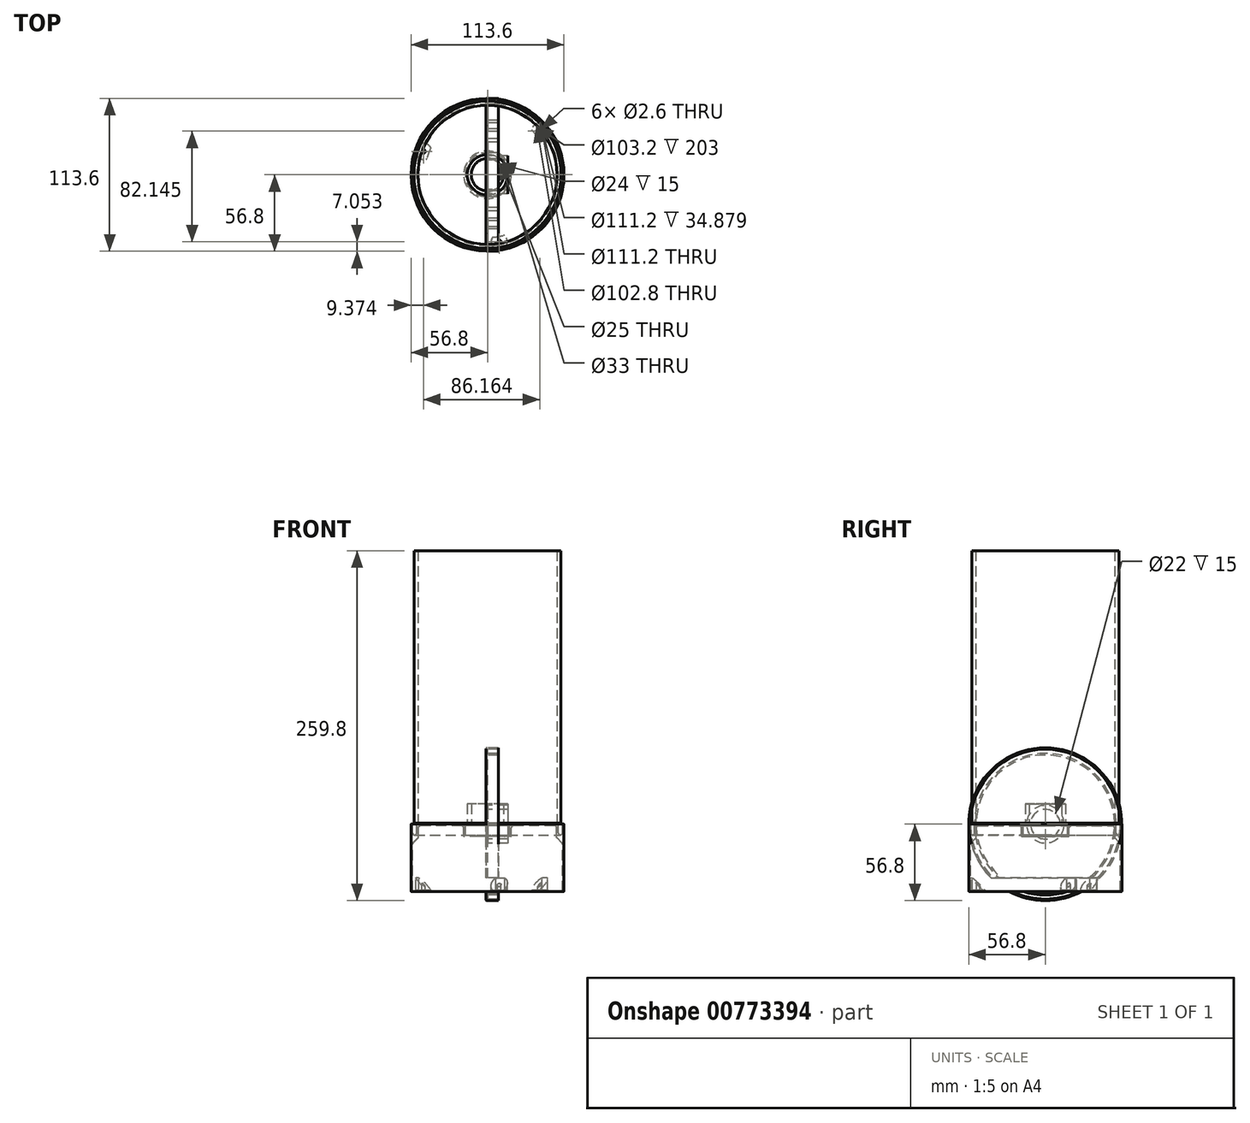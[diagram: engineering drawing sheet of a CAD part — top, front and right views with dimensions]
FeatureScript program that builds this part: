
annotation { "Feature Type Name" : "Feature", "Feature Type Description" : "" }
export const myFeature = defineFeature(function(context is Context, id is Id, definition is map)
    precondition{}
    {
        {
            var Q0;
            Q0=qCreatedBy(makeId("Front.planeOp"),FACE);
            var sketch = newSketch(context, id + "F0", { "sketchPlane" : qUnion([Q0])});
            skLineSegment(sketch, "E0", {"start": v(-56.8, 0) * mm, "end": v(-55.6, 0) * mm});
            skLineSegment(sketch, "E1", {"start": v(-55.6, 0) * mm, "end": v(-55.6, -8) * mm});
            skLineSegment(sketch, "E2", {"start": v(-55.6, -8) * mm, "end": v(-52.6, -8) * mm});
            skLineSegment(sketch, "E3", {"start": v(-52.6, -8) * mm, "end": v(-52.6, 0) * mm});
            skLineSegment(sketch, "E4", {"start": v(-52.6, 0) * mm, "end": v(-51.4, 0) * mm});
            skLineSegment(sketch, "E5", {"start": v(-51.4, 0) * mm, "end": v(-51.4, -10) * mm});
            skLineSegment(sketch, "E6", {"start": v(-51.4, -10) * mm, "end": v(-55.6, -14.2) * mm});
            skLineSegment(sketch, "E7", {"start": v(-55.6, -14.2) * mm, "end": v(-55.6, -50) * mm});
            skLineSegment(sketch, "E8", {"start": v(-55.6, -50) * mm, "end": v(-56.8, -50) * mm});
            skLineSegment(sketch, "E9", {"start": v(-56.8, -50) * mm, "end": v(-56.8, 0) * mm});
            skLineSegment(sketch, "E10", {"start": v(0, 0) * mm, "end": v(0, -50) * mm, "construction": true});
            skLineSegment(sketch, "E11", {"start": v(-52.6, -8) * mm, "end": v(0, -8) * mm, "construction": true});
            skLineSegment(sketch, "E12", {"start": v(-51.4, 0) * mm, "end": v(-16.5, 0) * mm});
            skLineSegment(sketch, "E13", {"start": v(-16.5, 0) * mm, "end": v(-16.5, -8) * mm});
            skLineSegment(sketch, "E14", {"start": v(-16.5, -8) * mm, "end": v(-12.5, -8) * mm});
            skLineSegment(sketch, "E15", {"start": v(-12.5, -8) * mm, "end": v(-12.5, -9.2) * mm});
            skLineSegment(sketch, "E16", {"start": v(-12.5, -9.2) * mm, "end": v(-17.7, -9.2) * mm});
            skLineSegment(sketch, "E17", {"start": v(-17.7, -9.2) * mm, "end": v(-17.7, -1.2) * mm});
            skLineSegment(sketch, "E18", {"start": v(-17.7, -1.2) * mm, "end": v(-51.4, -1.2) * mm});
            skLineSegment(sketch, "E19", {"start": v(-55.6, -40) * mm, "end": v(-45.6, -50) * mm});
            skLineSegment(sketch, "E20", {"start": v(-45.6, -50) * mm, "end": v(0, -50) * mm});
            skLineSegment(sketch, "E21", {"start": v(0, -50) * mm, "end": v(0, -40) * mm});
            skLineSegment(sketch, "E22", {"start": v(0, -40) * mm, "end": v(-55.6, -40) * mm});
            skLineSegment(sketch, "E23", {"start": v(-12.5, -8) * mm, "end": v(0, -8) * mm});
            skLineSegment(sketch, "E24", {"start": v(0, -8.3) * mm, "end": v(-12.5, -8.3) * mm});
            skLineSegment(sketch, "E25", {"start": v(0, -8) * mm, "end": v(0, -8.3) * mm});
            skSolve(sketch);
        }
        {
            var Q0;
            Q0=makeQuery(id+"F0.imprint","IMPRINT",FACE,{"disambiguationData":[TD([[makeQuery(id+"F0.imprint","IMPRINT",EDGE,{"derivedFrom":sQuery(id+"F0.wireOp",EDGE,"E0")}),-1.0]])]});
            var Q1;
            {var subQ1=sQuery(id+"F0.wireOp",EDGE,"E12");Q1=makeQuery(id+"F0.imprint","IMPRINT",FACE,{"disambiguationData":[TD([[makeQuery(id+"F0.imprint","IMPRINT",EDGE,{"derivedFrom":subQ1}),-1.0]])]});}
            var Q2;
            {var subQ0=sQuery(id+"F0.wireOp",EDGE,"E23");Q2=makeQuery(id+"F0.imprint","IMPRINT",FACE,{"disambiguationData":[TD([[makeQuery(id+"F0.imprint","IMPRINT",EDGE,{"derivedFrom":subQ0}),-1.0]])]});}
            var Q3;
            Q3=sQuery(id+"F0.wireOp",EDGE,"E10");
            revolve(context, id + "F1", {"surfaceOperationType" : NewSurfaceOperationType.NEW, "entities" : qUnion([Q0, Q1, Q2]), "axis" : qUnion([Q3]), "revolveType" : RevolveType.FULL});
        }
        {
            var Q0;
            Q0=qCreatedBy(makeId("Top.planeOp"),FACE);
            var sketch = newSketch(context, id + "F2", { "sketchPlane" : qUnion([Q0])});
            skCircle(sketch, "E26", {"center": v(0, 0) * mm, "radius": 55.5 * mm});
            skCircle(sketch, "E27", {"center": v(0, 0) * mm, "radius": 50.5 * mm, "construction": true});
            skCircle(sketch, "E28", {"center": v(-47.43, 17.35) * mm, "radius": 1.3 * mm});
            skCircle(sketch, "E29", {"center": v(-47.43, 17.35) * mm, "radius": 6 * mm});
            skCircle(sketch, "E30.1.0", {"center": v(8.69, -49.75) * mm, "radius": 1.3 * mm});
            skCircle(sketch, "E30.1.1", {"center": v(8.69, -49.75) * mm, "radius": 6 * mm});
            skCircle(sketch, "E30.2.0", {"center": v(38.74, 32.4) * mm, "radius": 1.3 * mm});
            skCircle(sketch, "E30.2.1", {"center": v(38.74, 32.4) * mm, "radius": 6 * mm});
            skCircle(sketch, "E31", {"center": v(0, 0) * mm, "radius": 15 * mm});
            skCircle(sketch, "E32", {"center": v(0, 0) * mm, "radius": 12 * mm});
            skSolve(sketch);
        }
        {
            var Q0;
            Q0=makeQuery(id+"F2.imprint","IMPRINT",FACE,{"disambiguationData":[TD([[makeQuery(id+"F2.imprint","IMPRINT",EDGE,{"derivedFrom":sQuery(id+"F2.wireOp",EDGE,"E26")}),1.0]])]});
            var Q1;
            Q1=makeQuery(id+"F2.imprint","IMPRINT",FACE,{"disambiguationData":[TD([[makeQuery(id+"F2.imprint","IMPRINT",EDGE,{"derivedFrom":sQuery(id+"F2.wireOp",EDGE,"E28")}),-1.0]])]});
            var Q2;
            Q2=makeQuery(id+"F2.imprint","IMPRINT",FACE,{"disambiguationData":[TD([[makeQuery(id+"F2.imprint","IMPRINT",EDGE,{"derivedFrom":sQuery(id+"F2.wireOp",EDGE,"E30.2.0")}),-1.0]])]});
            var Q3;
            Q3=makeQuery(id+"F2.imprint","IMPRINT",FACE,{"disambiguationData":[TD([[makeQuery(id+"F2.imprint","IMPRINT",EDGE,{"derivedFrom":sQuery(id+"F2.wireOp",EDGE,"E30.1.0")}),-1.0]])]});
            var Q4;
            Q4=makeQuery(id+"F2.imprint","IMPRINT",FACE,{"disambiguationData":[TD([[makeQuery(id+"F2.imprint","IMPRINT",EDGE,{"derivedFrom":sQuery(id+"F2.wireOp",EDGE,"E31")}),1.0]])]});
            extrude(context, id + "F3", {"entities" : qUnion([Q0, Q1, Q2, Q3, Q4]), "depth" : 0.9 * mm, "offsetDistance" : 25 * mm});
        }
        {
            var Q0;
            Q0=makeQuery(id+"F2.imprint","IMPRINT",FACE,{"disambiguationData":[TD([[makeQuery(id+"F2.imprint","IMPRINT",EDGE,{"derivedFrom":sQuery(id+"F2.wireOp",EDGE,"E30.1.0")}),-1.0]])]});
            var Q1;
            Q1=makeQuery(id+"F2.imprint","IMPRINT",FACE,{"disambiguationData":[TD([[makeQuery(id+"F2.imprint","IMPRINT",EDGE,{"derivedFrom":sQuery(id+"F2.wireOp",EDGE,"E28")}),-1.0]])]});
            var Q2;
            Q2=makeQuery(id+"F2.imprint","IMPRINT",FACE,{"disambiguationData":[TD([[makeQuery(id+"F2.imprint","IMPRINT",EDGE,{"derivedFrom":sQuery(id+"F2.wireOp",EDGE,"E30.2.0")}),-1.0]])]});
            var Q3;
            {var subQ0=sQuery(id+"F2.wireOp",EDGE,"E30.2.1");var subQ1=sQuery(id+"F2.wireOp",EDGE,"E26");var subQ2=makeQuery(id+"F2.imprint","INTERSECT",VERTEX,{"disambiguationData":[OD(0.0)],"derivedFrom":[subQ1,subQ0]});Q3=makeQuery(id+"F2.imprint","IMPRINT",FACE,{"disambiguationData":[TD([[makeQuery(id+"F2.imprint","IMPRINT",EDGE,{"disambiguationData":[TD([[subQ2,1.0]])],"derivedFrom":subQ1}),-1.0]])]});}
            var Q4;
            {var subQ0=sQuery(id+"F2.wireOp",EDGE,"E29");var subQ1=sQuery(id+"F2.wireOp",EDGE,"E26");var subQ2=makeQuery(id+"F2.imprint","INTERSECT",VERTEX,{"disambiguationData":[OD(0.0)],"derivedFrom":[subQ1,subQ0]});Q4=makeQuery(id+"F2.imprint","IMPRINT",FACE,{"disambiguationData":[TD([[makeQuery(id+"F2.imprint","IMPRINT",EDGE,{"disambiguationData":[TD([[subQ2,-1.0]])],"derivedFrom":subQ1}),-1.0]])]});}
            var Q5;
            {var subQ0=sQuery(id+"F2.wireOp",EDGE,"E30.1.1");var subQ1=sQuery(id+"F2.wireOp",EDGE,"E26");var subQ2=makeQuery(id+"F2.imprint","INTERSECT",VERTEX,{"disambiguationData":[OD(0.0)],"derivedFrom":[subQ1,subQ0]});Q5=makeQuery(id+"F2.imprint","IMPRINT",FACE,{"disambiguationData":[TD([[makeQuery(id+"F2.imprint","IMPRINT",EDGE,{"disambiguationData":[TD([[subQ2,-1.0]])],"derivedFrom":subQ1}),-1.0]])]});}
            extrude(context, id + "F4", {"entities" : qUnion([Q0, Q1, Q2, Q3, Q4, Q5]), "operationType" : NewBodyOperationType.ADD, "oppositeDirection" : true, "depth" : 49 * mm, "offsetDistance" : 25 * mm, "hasSecondDirection" : true, "secondDirectionOppositeDirection" : true, "secondDirectionDepth" : 40 * mm});
        }
        {
            var Q0;
            Q0=makeQuery(id+"F2.imprint","IMPRINT",FACE,{"disambiguationData":[TD([[makeQuery(id+"F2.imprint","IMPRINT",EDGE,{"derivedFrom":sQuery(id+"F2.wireOp",EDGE,"E31")}),1.0]])]});
            extrude(context, id + "F5", {"entities" : qUnion([Q0]), "operationType" : NewBodyOperationType.ADD, "depth" : 15 * mm, "offsetDistance" : 25 * mm});
        }
        {
            var Q0;
            Q0=qCreatedBy(makeId("Front.planeOp"),FACE);
            var sketch = newSketch(context, id + "F6", { "sketchPlane" : qUnion([Q0])});
            skLineSegment(sketch, "E33", {"start": v(-1.2, 0) * mm, "end": v(0, 0) * mm});
            skLineSegment(sketch, "E34", {"start": v(0, 0) * mm, "end": v(0, 51.4) * mm});
            skLineSegment(sketch, "E35", {"start": v(0, 51.4) * mm, "end": v(8, 51.4) * mm});
            skLineSegment(sketch, "E36", {"start": v(8, 51.4) * mm, "end": v(8, 52.6) * mm});
            skLineSegment(sketch, "E37", {"start": v(8, 52.6) * mm, "end": v(0, 52.6) * mm});
            skLineSegment(sketch, "E38", {"start": v(0, 52.6) * mm, "end": v(0, 55.6) * mm});
            skLineSegment(sketch, "E39", {"start": v(0, 55.6) * mm, "end": v(8, 55.6) * mm});
            skLineSegment(sketch, "E40", {"start": v(8, 55.6) * mm, "end": v(8, 56.8) * mm});
            skLineSegment(sketch, "E41", {"start": v(8, 56.8) * mm, "end": v(-1.2, 56.8) * mm});
            skLineSegment(sketch, "E42", {"start": v(-1.2, 56.8) * mm, "end": v(-1.2, 0) * mm});
            skLineSegment(sketch, "E43", {"start": v(15, 14) * mm, "end": v(0, 14) * mm});
            skLineSegment(sketch, "E44", {"start": v(0, 11) * mm, "end": v(15, 11) * mm});
            skLineSegment(sketch, "E45", {"start": v(15, 11) * mm, "end": v(15, 14) * mm});
            skSolve(sketch);
        }
        {
            var Q0;
            {var subQ0=sQuery(id+"F6.wireOp",EDGE,"E33");Q0=makeQuery(id+"F6.imprint","IMPRINT",FACE,{"disambiguationData":[TD([[makeQuery(id+"F6.imprint","IMPRINT",EDGE,{"derivedFrom":subQ0}),1.0]])]});}
            var Q1;
            {var subQ0=sQuery(id+"F6.wireOp",EDGE,"7EhCI0Yd-pM6g-tVcl-0YxW-UaFvZxdvcXcx");Q1=makeQuery(id+"F6.imprint","IMPRINT",FACE,{"disambiguationData":[TD([[makeQuery(id+"F6.imprint","IMPRINT",EDGE,{"derivedFrom":subQ0}),1.0]])]});}
            var Q2;
            {var subQ0=sQuery(id+"F6.wireOp",EDGE,"E43");Q2=makeQuery(id+"F6.imprint","IMPRINT",FACE,{"disambiguationData":[TD([[makeQuery(id+"F6.imprint","IMPRINT",EDGE,{"derivedFrom":subQ0}),1.0]])]});}
            var Q3;
            Q3=sQuery(id+"F6.wireOp",EDGE,"E33");
            revolve(context, id + "F7", {"surfaceOperationType" : NewSurfaceOperationType.NEW, "entities" : qUnion([Q0, Q1, Q2]), "axis" : qUnion([Q3]), "revolveType" : RevolveType.FULL});
        }
        {
            var Q0;
            Q0=qCreatedBy(makeId("Top.planeOp"),FACE);
            var sketch = newSketch(context, id + "F8", { "sketchPlane" : qUnion([Q0])});
            skCircle(sketch, "E46", {"center": v(0, 0) * mm, "radius": 51.6 * mm});
            skCircle(sketch, "E47", {"center": v(0, 0) * mm, "radius": 54.6 * mm});
            skSolve(sketch);
        }
        {
            var Q0;
            Q0=makeQuery(id+"F8.imprint","IMPRINT",FACE,{"disambiguationData":[TD([[makeQuery(id+"F8.imprint","IMPRINT",EDGE,{"derivedFrom":sQuery(id+"F8.wireOp",EDGE,"E46")}),-1.0]])]});
            extrude(context, id + "F9", {"entities" : qUnion([Q0]), "depth" : 203 * mm, "offsetDistance" : 25 * mm});
        }
        {
            var Q0;
            Q0=makeQuery(id+"F7.opRevolve","SWEPT_EDGE",EDGE,{"disambiguationData":[OSD([sQuery(id+"F6.wireOp",EDGE,"E41"),sQuery(id+"F6.wireOp",EDGE,"E42")])]});
            fillet(context, id + "F10", {"entities" : qUnion([Q0]), "radius" : 0.9 * mm, "tangentPropagation" : true, "allowEdgeOverflow" : false});
        }
        {
            var Q0;
            Q0=makeQuery(id+"F1.opRevolve","SWEPT_EDGE",EDGE,{"disambiguationData":[OSD([sQuery(id+"F0.wireOp",EDGE,"E0"),sQuery(id+"F0.wireOp",EDGE,"E9")])]});
            var Q1;
            Q1=makeQuery(id+"F1.opRevolve","SWEPT_EDGE",EDGE,{"disambiguationData":[OSD([sQuery(id+"F0.wireOp",EDGE,"E3"),sQuery(id+"F0.wireOp",EDGE,"E4")])]});
            var Q2;
            Q2=makeQuery(id+"F1.opRevolve","SWEPT_EDGE",EDGE,{"disambiguationData":[OSD([sQuery(id+"F0.wireOp",EDGE,"E0"),sQuery(id+"F0.wireOp",EDGE,"E1")])]});
            fillet(context, id + "F11", {"entities" : qUnion([Q0, Q1, Q2]), "radius" : 0.3 * mm, "tangentPropagation" : true, "allowEdgeOverflow" : false});
        }
        {
            var Q0;
            Q0=makeQuery(id+"F1.opRevolve","SWEPT_EDGE",EDGE,{"disambiguationData":[OSD([sQuery(id+"F0.wireOp",EDGE,"E1"),sQuery(id+"F0.wireOp",EDGE,"E2")])]});
            var Q1;
            Q1=makeQuery(id+"F1.opRevolve","SWEPT_EDGE",EDGE,{"disambiguationData":[OSD([sQuery(id+"F0.wireOp",EDGE,"E2"),sQuery(id+"F0.wireOp",EDGE,"E3")])]});
            fillet(context, id + "F12", {"entities" : qUnion([Q0, Q1]), "radius" : 1.5 * mm, "tangentPropagation" : true, "allowEdgeOverflow" : false});
        }
        {
            var Q0;
            Q0=makeQuery(id+"F1.opRevolve","SWEPT_EDGE",EDGE,{"disambiguationData":[OSD([sQuery(id+"F0.wireOp",EDGE,"E12"),sQuery(id+"F0.wireOp",EDGE,"E13")])]});
            var Q1;
            Q1=makeQuery(id+"F1.opRevolve","SWEPT_EDGE",EDGE,{"disambiguationData":[OSD([sQuery(id+"F0.wireOp",EDGE,"E14"),sQuery(id+"F0.wireOp",EDGE,"E15")])]});
            fillet(context, id + "F13", {"entities" : qUnion([Q0, Q1]), "radius" : 0.3 * mm, "tangentPropagation" : true, "allowEdgeOverflow" : false});
        }
        {
            var Q0;
            Q0=makeQuery(id+"F1.opRevolve","SWEPT_EDGE",EDGE,{"disambiguationData":[OSD([sQuery(id+"F0.wireOp",EDGE,"E16"),sQuery(id+"F0.wireOp",EDGE,"E17")])]});
            var Q1;
            Q1=makeQuery(id+"F1.opRevolve","SWEPT_EDGE",EDGE,{"disambiguationData":[OSD([sQuery(id+"F0.wireOp",EDGE,"E15"),sQuery(id+"F0.wireOp",EDGE,"E16")])]});
            fillet(context, id + "F14", {"entities" : qUnion([Q0, Q1]), "radius" : 0.3 * mm, "tangentPropagation" : true, "allowEdgeOverflow" : false});
        }
        {
            var Q0;
            Q0=makeQuery(id+"F1.opRevolve","SWEPT_EDGE",EDGE,{"disambiguationData":[OSD([sQuery(id+"F0.wireOp",EDGE,"E17"),sQuery(id+"F0.wireOp",EDGE,"E18")])]});
            var Q1;
            Q1=makeQuery(id+"F1.opRevolve","SWEPT_EDGE",EDGE,{"disambiguationData":[OSD([sQuery(id+"F0.wireOp",EDGE,"E5"),sQuery(id+"F0.wireOp",EDGE,"E18")])]});
            var Q2;
            Q2=makeQuery(id+"F1.opRevolve","SWEPT_EDGE",EDGE,{"disambiguationData":[OSD([sQuery(id+"F0.wireOp",EDGE,"E6"),sQuery(id+"F0.wireOp",EDGE,"E7")])]});
            fillet(context, id + "F15", {"entities" : qUnion([Q0, Q1, Q2]), "radius" : 1.5 * mm, "tangentPropagation" : true, "allowEdgeOverflow" : false});
        }
        {
            var Q0;
            Q0=makeQuery(id+"F1.opRevolve","SWEPT_EDGE",EDGE,{"disambiguationData":[OSD([sQuery(id+"F0.wireOp",EDGE,"E5"),sQuery(id+"F0.wireOp",EDGE,"E6")])]});
            var Q1;
            Q1=makeQuery(id+"F1.opRevolve","SWEPT_EDGE",EDGE,{"disambiguationData":[OSD([sQuery(id+"F0.wireOp",EDGE,"E7"),sQuery(id+"F0.wireOp",EDGE,"E8")])]});
            var Q2;
            Q2=makeQuery(id+"F1.opRevolve","SWEPT_EDGE",EDGE,{"disambiguationData":[OSD([sQuery(id+"F0.wireOp",EDGE,"E8"),sQuery(id+"F0.wireOp",EDGE,"E9")])]});
            var Q3;
            Q3=makeQuery(id+"F4.opExtrude","CAP_EDGE",EDGE,{"disambiguationData":[OSD([sQuery(id+"F2.wireOp",EDGE,"E30.2.1")])],"isStart":false});
            var Q4;
            Q4=makeQuery(id+"F4.opExtrude","CAP_EDGE",EDGE,{"disambiguationData":[OSD([sQuery(id+"F2.wireOp",EDGE,"E30.2.1")])],"isStart":true});
            var Q5;
            Q5=makeQuery(id+"F4.opExtrude","CAP_EDGE",EDGE,{"disambiguationData":[OSD([sQuery(id+"F2.wireOp",EDGE,"E30.2.0")])],"isStart":false});
            var Q6;
            Q6=makeQuery(id+"F4.opExtrude","CAP_EDGE",EDGE,{"disambiguationData":[OSD([sQuery(id+"F2.wireOp",EDGE,"E28")])],"isStart":false});
            var Q7;
            Q7=makeQuery(id+"F4.opExtrude","CAP_EDGE",EDGE,{"disambiguationData":[OSD([sQuery(id+"F2.wireOp",EDGE,"E29")])],"isStart":false});
            var Q8;
            Q8=makeQuery(id+"F4.opExtrude","CAP_EDGE",EDGE,{"disambiguationData":[OSD([sQuery(id+"F2.wireOp",EDGE,"E29")])],"isStart":true});
            var Q9;
            Q9=makeQuery(id+"F4.opExtrude","CAP_EDGE",EDGE,{"disambiguationData":[OSD([sQuery(id+"F2.wireOp",EDGE,"E30.1.0")])],"isStart":false});
            var Q10;
            Q10=makeQuery(id+"F4.opExtrude","CAP_EDGE",EDGE,{"disambiguationData":[OSD([sQuery(id+"F2.wireOp",EDGE,"E30.1.1")])],"isStart":false});
            var Q11;
            Q11=makeQuery(id+"F4.opExtrude","CAP_EDGE",EDGE,{"disambiguationData":[OSD([sQuery(id+"F2.wireOp",EDGE,"E30.1.1")])],"isStart":true});
            fillet(context, id + "F16", {"entities" : qUnion([Q0, Q1, Q2, Q3, Q4, Q5, Q6, Q7, Q8, Q9, Q10, Q11]), "radius" : 0.3 * mm, "tangentPropagation" : true, "allowEdgeOverflow" : false});
        }
        {
            var Q0;
            Q0=makeQuery(id+"F4.opExtrude","CAP_EDGE",EDGE,{"disambiguationData":[OSD([sQuery(id+"F2.wireOp",EDGE,"E30.2.0")])],"isStart":true});
            var Q1;
            Q1=makeQuery(id+"F4.opExtrude","CAP_EDGE",EDGE,{"disambiguationData":[OSD([sQuery(id+"F2.wireOp",EDGE,"E30.1.0")])],"isStart":true});
            var Q2;
            Q2=makeQuery(id+"F4.opExtrude","CAP_EDGE",EDGE,{"disambiguationData":[OSD([sQuery(id+"F2.wireOp",EDGE,"E28")])],"isStart":true});
            fillet(context, id + "F17", {"entities" : qUnion([Q0, Q1, Q2]), "radius" : 0.3 * mm, "tangentPropagation" : true, "allowEdgeOverflow" : false});
        }
        {
            var Q0;
            Q0=makeQuery(id+"F0.imprint","IMPRINT",FACE,{"disambiguationData":[TD([[makeQuery(id+"F0.imprint","IMPRINT",EDGE,{"derivedFrom":sQuery(id+"F0.wireOp",EDGE,"E19")}),1.0]])]});
            var Q1;
            Q1=sQuery(id+"F0.wireOp",EDGE,"E21");
            revolve(context, id + "F18", {"operationType" : NewBodyOperationType.REMOVE, "surfaceOperationType" : NewSurfaceOperationType.NEW, "entities" : qUnion([Q0]), "axis" : qUnion([Q1]), "revolveType" : RevolveType.FULL, "oppositeDirection" : true});
        }
    });
